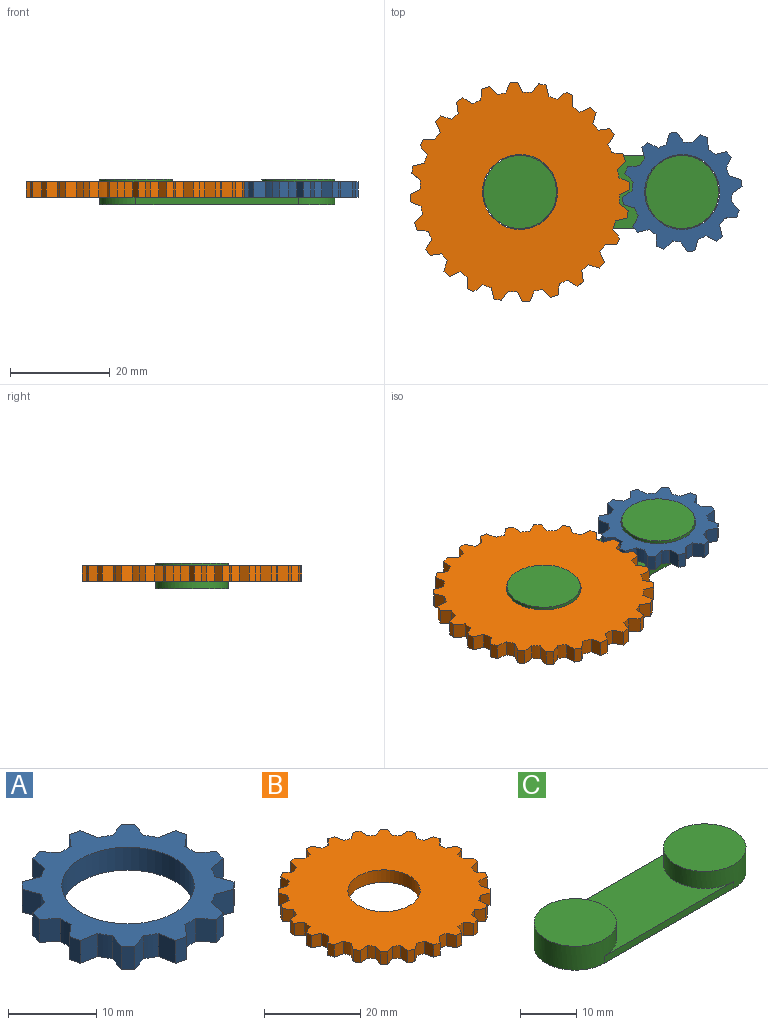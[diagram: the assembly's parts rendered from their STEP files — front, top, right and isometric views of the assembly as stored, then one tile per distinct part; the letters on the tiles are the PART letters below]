
ASSEMBLY  parts=3 mates=2
PART A: 51 faces, bbox 23.6x23.6x3.2 mm
  f0: plane 3.18x2.34mm, normal (-0.17,0.98,0), area 7.6mm2, adj f1,f47,f49,f50
  f1: plane 3.18x1.45mm, normal (-0.97,0.26,0), area 4.8mm2, adj f0,f2,f49,f50
  f2: plane 3.18x1.82mm, normal (-0.64,-0.77,0), area 7.6mm2, adj f1,f3,f49,f50
  f3: cylinder r=10mm len=3.18mm, axis (0,0,-1), area 5.4mm2, adj f2,f4,f49,f50
  f4: plane 3.18x1.82mm, normal (-0.64,0.77,0), area 7.6mm2, adj f3,f5,f49,f50
  f5: plane 3.18x1.45mm, normal (-0.97,-0.26,0), area 4.8mm2, adj f4,f6,f49,f50
  f6: plane 3.18x2.34mm, normal (-0.17,-0.98,0), area 7.6mm2, adj f5,f7,f49,f50
  f7: cylinder r=10mm len=3.18mm, axis (0,0,-1), area 5.4mm2, adj f6,f8,f49,f50
  f8: plane 3.18x2.23mm, normal (-0.94,0.34,0), area 7.6mm2, adj f7,f9,f49,f50
  f9: plane 3.18x1.06mm, normal (-0.71,-0.71,0), area 4.8mm2, adj f8,f10,f49,f50
  f10: plane 3.18x2.23mm, normal (0.34,-0.94,0), area 7.6mm2, adj f9,f11,f49,f50
  f11: cylinder r=10mm len=3.18mm, axis (0,0,-1), area 5.4mm2, adj f10,f12,f49,f50
  f12: plane 3.18x2.34mm, normal (-0.98,-0.17,0), area 7.6mm2, adj f11,f13,f49,f50
  f13: plane 3.18x1.45mm, normal (-0.26,-0.97,0), area 4.8mm2, adj f12,f14,f49,f50
  f14: plane 3.18x1.82mm, normal (0.77,-0.64,0), area 7.6mm2, adj f13,f15,f49,f50
  f15: cylinder r=10mm len=3.18mm, axis (0,0,-1), area 5.4mm2, adj f14,f16,f49,f50
  f16: plane 3.18x1.82mm, normal (-0.77,-0.64,0), area 7.6mm2, adj f15,f17,f49,f50
  f17: plane 3.18x1.45mm, normal (0.26,-0.97,0), area 4.8mm2, adj f16,f18,f49,f50
  f18: plane 3.18x2.34mm, normal (0.98,-0.17,0), area 7.6mm2, adj f17,f19,f49,f50
  f19: cylinder r=10mm len=3.18mm, axis (0,0,-1), area 5.4mm2, adj f18,f20,f49,f50
  f20: plane 3.18x2.23mm, normal (-0.34,-0.94,0), area 7.6mm2, adj f19,f21,f49,f50
  f21: plane 3.18x1.06mm, normal (0.71,-0.71,0), area 4.8mm2, adj f20,f22,f49,f50
  f22: plane 3.18x2.23mm, normal (0.94,0.34,0), area 7.6mm2, adj f21,f23,f49,f50
  f23: cylinder r=10mm len=3.18mm, axis (0,0,-1), area 5.4mm2, adj f22,f24,f49,f50
  f24: plane 3.18x2.34mm, normal (0.17,-0.98,0), area 7.6mm2, adj f23,f25,f49,f50
  f25: plane 3.18x1.45mm, normal (0.97,-0.26,0), area 4.8mm2, adj f24,f26,f49,f50
  f26: plane 3.18x1.82mm, normal (0.64,0.77,0), area 7.6mm2, adj f25,f27,f49,f50
  f27: cylinder r=10mm len=3.18mm, axis (0,0,-1), area 5.4mm2, adj f26,f28,f49,f50
  f28: plane 3.18x1.82mm, normal (0.64,-0.77,0), area 7.6mm2, adj f27,f29,f49,f50
  f29: plane 3.18x1.45mm, normal (0.97,0.26,0), area 4.8mm2, adj f28,f30,f49,f50
  f30: plane 3.18x2.34mm, normal (0.17,0.98,0), area 7.6mm2, adj f29,f31,f49,f50
  f31: cylinder r=10mm len=3.18mm, axis (0,0,-1), area 5.4mm2, adj f30,f32,f49,f50
  f32: plane 3.18x2.23mm, normal (0.94,-0.34,0), area 7.6mm2, adj f31,f33,f49,f50
  f33: plane 3.18x1.06mm, normal (0.71,0.71,0), area 4.8mm2, adj f32,f34,f49,f50
  f34: plane 3.18x2.23mm, normal (-0.34,0.94,0), area 7.6mm2, adj f33,f35,f49,f50
  f35: cylinder r=10mm len=3.18mm, axis (0,0,-1), area 5.4mm2, adj f34,f36,f49,f50
  f36: plane 3.18x2.34mm, normal (0.98,0.17,0), area 7.6mm2, adj f35,f37,f49,f50
  f37: plane 3.18x1.45mm, normal (0.26,0.97,0), area 4.8mm2, adj f36,f38,f49,f50
  f38: plane 3.18x1.82mm, normal (-0.77,0.64,0), area 7.6mm2, adj f37,f39,f49,f50
  f39: cylinder r=10mm len=3.18mm, axis (0,0,-1), area 5.4mm2, adj f38,f40,f49,f50
  f40: plane 3.18x1.82mm, normal (0.77,0.64,0), area 7.6mm2, adj f39,f41,f49,f50
  f41: plane 3.18x1.45mm, normal (-0.26,0.97,0), area 4.8mm2, adj f40,f42,f49,f50
  f42: plane 3.18x2.34mm, normal (-0.98,0.17,0), area 7.6mm2, adj f41,f43,f49,f50
  f43: cylinder r=10mm len=3.18mm, axis (0,0,-1), area 5.4mm2, adj f42,f44,f49,f50
  f44: plane 3.18x2.23mm, normal (0.34,0.94,0), area 7.6mm2, adj f43,f45,f49,f50
  f45: plane 3.18x1.06mm, normal (-0.71,0.71,0), area 4.8mm2, adj f44,f46,f49,f50
  f46: plane 3.18x2.23mm, normal (-0.94,-0.34,0), area 7.6mm2, adj f45,f47,f49,f50
  f47: cylinder r=10mm len=3.18mm, axis (0,0,-1), area 5.4mm2, adj f0,f46,f49,f50
  f48: cylinder r=7.5mm len=15mm, axis (0,0,-1), area 149.6mm2, adj f49,f50
  f49: plane 23.57x23.57mm, normal (0,0,1), area 197.9mm2, adj f0,f1,f2,f3,f4,f5,f6,f7
  f50: plane 23.57x23.57mm, normal (0,0,-1), area 197.9mm2, adj f0,f1,f2,f3,f4,f5,f6,f7
PART B: 99 faces, bbox 44x44x3.2 mm
  f0: plane 3.18x2.15mm, normal (-0.34,-0.94,0), area 7.3mm2, adj f1,f95,f97,f98
  f1: plane 3.18x1.06mm, normal (0.71,-0.71,0), area 4.8mm2, adj f0,f2,f97,f98
  f2: plane 3.18x2.15mm, normal (0.94,0.34,0), area 7.3mm2, adj f1,f3,f97,f98
  f3: cylinder r=20mm len=3.18mm, axis (0,0,-1), area 5.7mm2, adj f2,f4,f97,f98
  f4: plane 3.18x2.28mm, normal (-0.09,-1,0), area 7.3mm2, adj f3,f5,f97,f98
  f5: plane 3.18x1.3mm, normal (0.87,-0.5,0), area 4.8mm2, adj f4,f6,f97,f98
  f6: plane 3.18x1.87mm, normal (0.82,0.57,0), area 7.3mm2, adj f5,f7,f97,f98
  f7: cylinder r=20mm len=3.18mm, axis (0,0,-1), area 5.7mm2, adj f6,f8,f97,f98
  f8: plane 3.18x2.25mm, normal (0.17,-0.98,0), area 7.3mm2, adj f7,f9,f97,f98
  f9: plane 3.18x1.45mm, normal (0.97,-0.26,0), area 4.8mm2, adj f8,f10,f97,f98
  f10: plane 3.18x1.75mm, normal (0.64,0.77,0), area 7.3mm2, adj f9,f11,f97,f98
  f11: cylinder r=20mm len=3.18mm, axis (0,0,-1), area 5.7mm2, adj f10,f12,f97,f98
  f12: plane 3.18x2.07mm, normal (0.42,-0.91,0), area 7.3mm2, adj f11,f13,f97,f98
  f13: plane 3.18x1.5mm, normal (1,0,0), area 4.8mm2, adj f12,f14,f97,f98
  f14: plane 3.18x2.07mm, normal (0.42,0.91,0), area 7.3mm2, adj f13,f15,f97,f98
  f15: cylinder r=20mm len=3.18mm, axis (0,0,-1), area 5.7mm2, adj f14,f16,f97,f98
  f16: plane 3.18x1.75mm, normal (0.64,-0.77,0), area 7.3mm2, adj f15,f17,f97,f98
  f17: plane 3.18x1.45mm, normal (0.97,0.26,0), area 4.8mm2, adj f16,f18,f97,f98
  f18: plane 3.18x2.25mm, normal (0.17,0.98,0), area 7.3mm2, adj f17,f19,f97,f98
  f19: cylinder r=20mm len=3.18mm, axis (0,0,-1), area 5.7mm2, adj f18,f20,f97,f98
  f20: plane 3.18x1.87mm, normal (0.82,-0.57,0), area 7.3mm2, adj f19,f21,f97,f98
  f21: plane 3.18x1.3mm, normal (0.87,0.5,0), area 4.8mm2, adj f20,f22,f97,f98
  f22: plane 3.18x2.28mm, normal (-0.09,1,0), area 7.3mm2, adj f21,f23,f97,f98
  f23: cylinder r=20mm len=3.18mm, axis (0,0,-1), area 5.7mm2, adj f22,f24,f97,f98
  f24: plane 3.18x2.15mm, normal (0.94,-0.34,0), area 7.3mm2, adj f23,f25,f97,f98
  f25: plane 3.18x1.06mm, normal (0.71,0.71,0), area 4.8mm2, adj f24,f26,f97,f98
  f26: plane 3.18x2.15mm, normal (-0.34,0.94,0), area 7.3mm2, adj f25,f27,f97,f98
  f27: cylinder r=20mm len=3.18mm, axis (0,0,-1), area 5.7mm2, adj f26,f28,f97,f98
  f28: plane 3.18x2.28mm, normal (1,-0.09,0), area 7.3mm2, adj f27,f29,f97,f98
  f29: plane 3.18x1.3mm, normal (0.5,0.87,0), area 4.8mm2, adj f28,f30,f97,f98
  f30: plane 3.18x1.87mm, normal (-0.57,0.82,0), area 7.3mm2, adj f29,f31,f97,f98
  f31: cylinder r=20mm len=3.18mm, axis (0,0,-1), area 5.7mm2, adj f30,f32,f97,f98
  f32: plane 3.18x2.25mm, normal (0.98,0.17,0), area 7.3mm2, adj f31,f33,f97,f98
  f33: plane 3.18x1.45mm, normal (0.26,0.97,0), area 4.8mm2, adj f32,f34,f97,f98
  f34: plane 3.18x1.75mm, normal (-0.77,0.64,0), area 7.3mm2, adj f33,f35,f97,f98
  f35: cylinder r=20mm len=3.18mm, axis (0,0,-1), area 5.7mm2, adj f34,f36,f97,f98
  f36: plane 3.18x2.07mm, normal (0.91,0.42,0), area 7.3mm2, adj f35,f37,f97,f98
  f37: plane 3.18x1.5mm, normal (0,1,0), area 4.8mm2, adj f36,f38,f97,f98
  f38: plane 3.18x2.07mm, normal (-0.91,0.42,0), area 7.3mm2, adj f37,f39,f97,f98
  f39: cylinder r=20mm len=3.18mm, axis (0,0,-1), area 5.7mm2, adj f38,f40,f97,f98
  f40: plane 3.18x1.75mm, normal (0.77,0.64,0), area 7.3mm2, adj f39,f41,f97,f98
  f41: plane 3.18x1.45mm, normal (-0.26,0.97,0), area 4.8mm2, adj f40,f42,f97,f98
  f42: plane 3.18x2.25mm, normal (-0.98,0.17,0), area 7.3mm2, adj f41,f43,f97,f98
  f43: cylinder r=20mm len=3.18mm, axis (0,0,-1), area 5.7mm2, adj f42,f44,f97,f98
  f44: plane 3.18x1.87mm, normal (0.57,0.82,0), area 7.3mm2, adj f43,f45,f97,f98
  f45: plane 3.18x1.3mm, normal (-0.5,0.87,0), area 4.8mm2, adj f44,f46,f97,f98
  f46: plane 3.18x2.28mm, normal (-1,-0.09,0), area 7.3mm2, adj f45,f47,f97,f98
  f47: cylinder r=20mm len=3.18mm, axis (0,0,-1), area 5.7mm2, adj f46,f48,f97,f98
  f48: plane 3.18x2.15mm, normal (0.34,0.94,0), area 7.3mm2, adj f47,f49,f97,f98
  f49: plane 3.18x1.06mm, normal (-0.71,0.71,0), area 4.8mm2, adj f48,f50,f97,f98
  f50: plane 3.18x2.15mm, normal (-0.94,-0.34,0), area 7.3mm2, adj f49,f51,f97,f98
  f51: cylinder r=20mm len=3.18mm, axis (0,0,-1), area 5.7mm2, adj f50,f52,f97,f98
  f52: plane 3.18x2.28mm, normal (0.09,1,0), area 7.3mm2, adj f51,f53,f97,f98
  f53: plane 3.18x1.3mm, normal (-0.87,0.5,0), area 4.8mm2, adj f52,f54,f97,f98
  f54: plane 3.18x1.87mm, normal (-0.82,-0.57,0), area 7.3mm2, adj f53,f55,f97,f98
  f55: cylinder r=20mm len=3.18mm, axis (0,0,-1), area 5.7mm2, adj f54,f56,f97,f98
  f56: plane 3.18x2.25mm, normal (-0.17,0.98,0), area 7.3mm2, adj f55,f57,f97,f98
  f57: plane 3.18x1.45mm, normal (-0.97,0.26,0), area 4.8mm2, adj f56,f58,f97,f98
  f58: plane 3.18x1.75mm, normal (-0.64,-0.77,0), area 7.3mm2, adj f57,f59,f97,f98
  f59: cylinder r=20mm len=3.18mm, axis (0,0,-1), area 5.7mm2, adj f58,f60,f97,f98
  f60: plane 3.18x2.07mm, normal (-0.42,0.91,0), area 7.3mm2, adj f59,f61,f97,f98
  f61: plane 3.18x1.5mm, normal (-1,0,0), area 4.8mm2, adj f60,f62,f97,f98
  f62: plane 3.18x2.07mm, normal (-0.42,-0.91,0), area 7.3mm2, adj f61,f63,f97,f98
  f63: cylinder r=20mm len=3.18mm, axis (0,0,-1), area 5.7mm2, adj f62,f64,f97,f98
  f64: plane 3.18x1.75mm, normal (-0.64,0.77,0), area 7.3mm2, adj f63,f65,f97,f98
  f65: plane 3.18x1.45mm, normal (-0.97,-0.26,0), area 4.8mm2, adj f64,f66,f97,f98
  f66: plane 3.18x2.25mm, normal (-0.17,-0.98,0), area 7.3mm2, adj f65,f67,f97,f98
  f67: cylinder r=20mm len=3.18mm, axis (0,0,-1), area 5.7mm2, adj f66,f68,f97,f98
  f68: plane 3.18x1.87mm, normal (-0.82,0.57,0), area 7.3mm2, adj f67,f69,f97,f98
  f69: plane 3.18x1.3mm, normal (-0.87,-0.5,0), area 4.8mm2, adj f68,f70,f97,f98
  f70: plane 3.18x2.28mm, normal (0.09,-1,0), area 7.3mm2, adj f69,f71,f97,f98
  f71: cylinder r=20mm len=3.18mm, axis (0,0,-1), area 5.7mm2, adj f70,f72,f97,f98
  f72: plane 3.18x2.15mm, normal (-0.94,0.34,0), area 7.3mm2, adj f71,f73,f97,f98
  f73: plane 3.18x1.06mm, normal (-0.71,-0.71,0), area 4.8mm2, adj f72,f74,f97,f98
  f74: plane 3.18x2.15mm, normal (0.34,-0.94,0), area 7.3mm2, adj f73,f75,f97,f98
  f75: cylinder r=20mm len=3.18mm, axis (0,0,-1), area 5.7mm2, adj f74,f76,f97,f98
  f76: plane 3.18x2.28mm, normal (-1,0.09,0), area 7.3mm2, adj f75,f77,f97,f98
  f77: plane 3.18x1.3mm, normal (-0.5,-0.87,0), area 4.8mm2, adj f76,f78,f97,f98
  f78: plane 3.18x1.87mm, normal (0.57,-0.82,0), area 7.3mm2, adj f77,f79,f97,f98
  f79: cylinder r=20mm len=3.18mm, axis (0,0,-1), area 5.7mm2, adj f78,f80,f97,f98
  f80: plane 3.18x2.25mm, normal (-0.98,-0.17,0), area 7.3mm2, adj f79,f81,f97,f98
  f81: plane 3.18x1.45mm, normal (-0.26,-0.97,0), area 4.8mm2, adj f80,f82,f97,f98
  f82: plane 3.18x1.75mm, normal (0.77,-0.64,0), area 7.3mm2, adj f81,f83,f97,f98
  f83: cylinder r=20mm len=3.18mm, axis (0,0,-1), area 5.7mm2, adj f82,f84,f97,f98
  f84: plane 3.18x2.07mm, normal (-0.91,-0.42,0), area 7.3mm2, adj f83,f85,f97,f98
  f85: plane 3.18x1.5mm, normal (0,-1,0), area 4.8mm2, adj f84,f86,f97,f98
  f86: plane 3.18x2.07mm, normal (0.91,-0.42,0), area 7.3mm2, adj f85,f87,f97,f98
  f87: cylinder r=20mm len=3.18mm, axis (0,0,-1), area 5.7mm2, adj f86,f88,f97,f98
  f88: plane 3.18x1.75mm, normal (-0.77,-0.64,0), area 7.3mm2, adj f87,f89,f97,f98
  f89: plane 3.18x1.45mm, normal (0.26,-0.97,0), area 4.8mm2, adj f88,f90,f97,f98
  f90: plane 3.18x2.25mm, normal (0.98,-0.17,0), area 7.3mm2, adj f89,f91,f97,f98
  f91: cylinder r=20mm len=3.18mm, axis (0,0,-1), area 5.7mm2, adj f90,f92,f97,f98
  f92: plane 3.18x1.87mm, normal (-0.57,-0.82,0), area 7.3mm2, adj f91,f93,f97,f98
  f93: plane 3.18x1.3mm, normal (0.5,-0.87,0), area 4.8mm2, adj f92,f94,f97,f98
  f94: plane 3.18x2.28mm, normal (1,0.09,0), area 7.3mm2, adj f93,f95,f97,f98
  f95: cylinder r=20mm len=3.18mm, axis (0,0,-1), area 5.7mm2, adj f0,f94,f97,f98
  f96: cylinder r=7.5mm len=15mm, axis (0,0,-1), area 149.6mm2, adj f97,f98
  f97: plane 44x44mm, normal (0,0,1), area 1198.7mm2, adj f0,f1,f2,f3,f4,f5,f6,f7
  f98: plane 44x44mm, normal (0,0,-1), area 1198.7mm2, adj f0,f1,f2,f3,f4,f5,f6,f7
PART C: 8 faces, bbox 47x14.6x5.2 mm
  f0: plane 32.45x14.6mm, normal (0,0,1), area 306.3mm2, adj f1,f2,f3,f4
  f1: plane 32.45x1.5mm, normal (0,-1,0), area 48.7mm2, adj f0,f2,f4,f5
  f2: cylinder r=7.3mm len=14.6mm, axis (0,0,1), area 203mm2, adj f0,f1,f3,f5,f6
  f3: plane 32.45x1.5mm, normal (0,1,0), area 48.7mm2, adj f0,f2,f4,f5
  f4: cylinder r=7.3mm len=14.6mm, axis (0,0,1), area 203mm2, adj f0,f1,f3,f5,f7
  f5: plane 47.05x14.6mm, normal (0,0,-1), area 641.2mm2, adj f1,f2,f3,f4
  f6: plane 14.6x14.6mm, normal (0,0,1), area 167.4mm2, adj f2
  f7: plane 14.6x14.6mm, normal (0,0,1), area 167.4mm2, adj f4
PLACE A rot(axis=(0,0,1),143.6deg) t=(58.56,-19.26,0)mm
PLACE B rot(axis=(0,0,1),108.2deg) t=(0,0,0)mm
PLACE C at identity fixed
MATE revolute A.f48 <-> C.f4  axis (0,0,-1) through (32.45,0,0)mm
MATE revolute B.f96 <-> C.f2  axis (0,0,-1) through (0,0,0)mm
